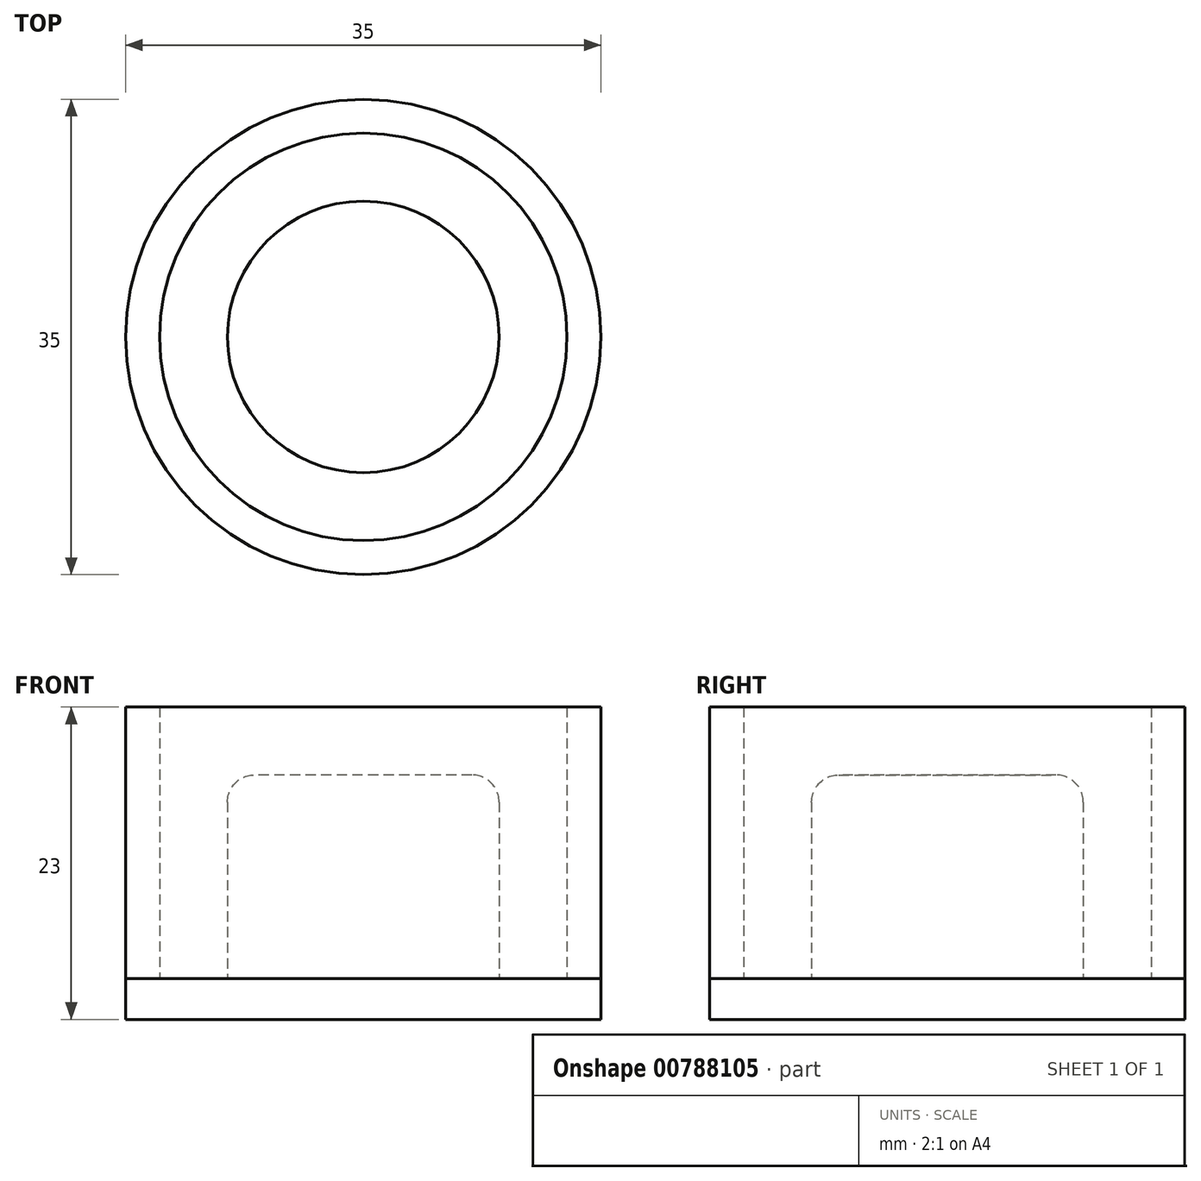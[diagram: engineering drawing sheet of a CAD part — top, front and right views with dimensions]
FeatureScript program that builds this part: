
annotation { "Feature Type Name" : "Feature", "Feature Type Description" : "" }
export const myFeature = defineFeature(function(context is Context, id is Id, definition is map)
    precondition{}
    {
        {
            var Q0;
            Q0=qCreatedBy(makeId("Top.planeOp"),FACE);
            var sketch = newSketch(context, id + "F0", { "sketchPlane" : qUnion([Q0])});
            skCircle(sketch, "E0", {"center": v(0, 0) * mm, "radius": 15 * mm});
            skCircle(sketch, "E1", {"center": v(0, 0) * mm, "radius": 17.5 * mm});
            skSolve(sketch);
        }
        {
            var Q0;
            Q0 = qSketchRegion(id + "F0", true);
            extrude(context, id + "F1", {"entities" : qUnion([Q0]), "depth" : 20 * mm, "offsetDistance" : 25 * mm});
        }
        {
            var Q0;
            Q0=qCreatedBy(makeId("Top.planeOp"),FACE);
            var sketch = newSketch(context, id + "F2", { "sketchPlane" : qUnion([Q0])});
            skCircle(sketch, "E2", {"center": v(0, 0) * mm, "radius": 10 * mm});
            skSolve(sketch);
        }
        {
            var Q0;
            Q0 = qSketchRegion(id + "F2", true);
            extrude(context, id + "F3", {"entities" : qUnion([Q0]), "depth" : 15 * mm, "offsetDistance" : 25 * mm});
        }
        {
            var Q0;
            Q0=qCreatedBy(makeId("Top.planeOp"),FACE);
            var sketch = newSketch(context, id + "F4", { "sketchPlane" : qUnion([Q0])});
            skCircle(sketch, "E3", {"center": v(0, 0) * mm, "radius": 17.5 * mm});
            skSolve(sketch);
        }
        {
            var Q0;
            Q0 = qSketchRegion(id + "F4", true);
            extrude(context, id + "F5", {"entities" : qUnion([Q0]), "oppositeDirection" : true, "depth" : 3 * mm, "offsetDistance" : 25 * mm});
        }
        {
            var Q0;
            Q0=makeQuery(id+"F3.opExtrude","CAP_EDGE",EDGE,{"disambiguationData":[OSD([sQuery(id+"F2.wireOp",EDGE,"E2")])],"isStart":false});
            fillet(context, id + "F6", {"entities" : qUnion([Q0]), "radius" : 2 * mm, "tangentPropagation" : true, "allowEdgeOverflow" : false});
        }
    });
